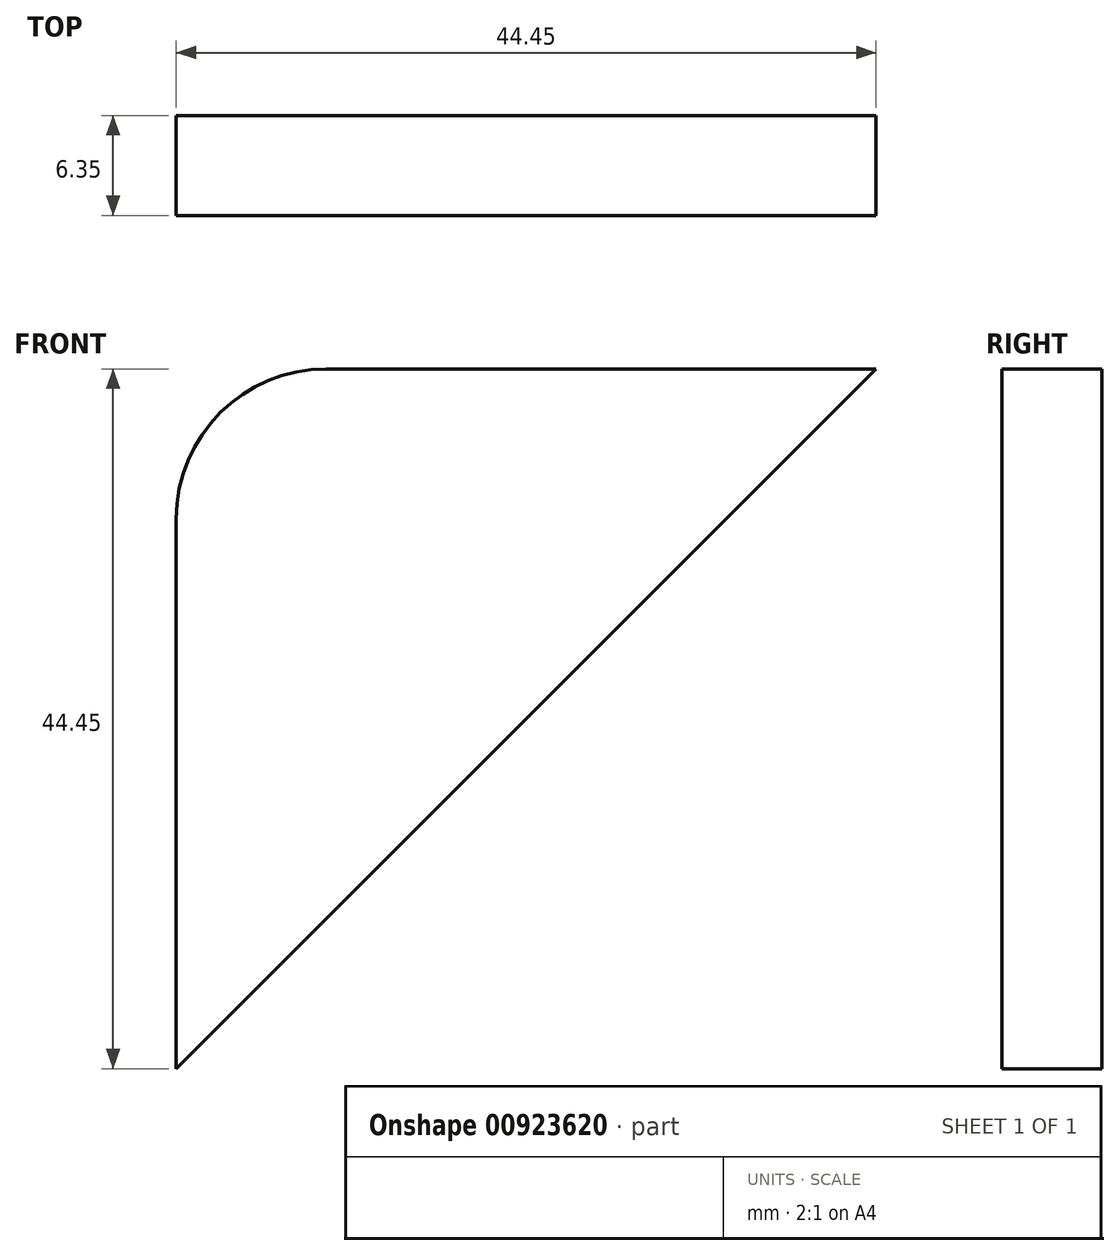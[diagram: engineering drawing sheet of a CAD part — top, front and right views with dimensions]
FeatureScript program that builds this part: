
annotation { "Feature Type Name" : "Feature", "Feature Type Description" : "" }
export const myFeature = defineFeature(function(context is Context, id is Id, definition is map)
    precondition{}
    {
        {
            var Q0;
            Q0=qCreatedBy(makeId("Front.planeOp"),FACE);
            var sketch = newSketch(context, id + "F0", { "sketchPlane" : qUnion([Q0])});
            skLineSegment(sketch, "E0", {"start": v(-34.04, -29.74) * mm, "end": v(-34.04, 5.19) * mm});
            skLineSegment(sketch, "E1", {"start": v(-24.51, 14.71) * mm, "end": v(10.41, 14.71) * mm});
            skPoint(sketch, "E2.visualSharp", {"position": v(-34.04, 14.71) * mm});
            skArc(sketch, "E2.filletArc", {"start": v(-24.51, 14.71) * mm, "mid": v(-31.25, 11.92) * mm, "end": v(-34.04, 5.19) * mm});
            skPoint(sketch, "E3.visualSharp", {"position": v(-43.56, 24.24) * mm});
            skArc(sketch, "E3.filletArc", {"start": v(-43.3, 24.24) * mm, "mid": v(-43.49, 24.16) * mm, "end": v(-43.56, 23.98) * mm});
            skLineSegment(sketch, "E4", {"start": v(-34.04, -29.74) * mm, "end": v(10.41, 14.71) * mm});
            skSolve(sketch);
        }
        {
            var Q0;
            Q0=qSketchRegion(id+"F0",true);
            extrude(context, id + "F1", {"entities" : qUnion([Q0]), "depth" : 6.35 * mm, "offsetDistance" : 25.4 * mm});
        }
    });
